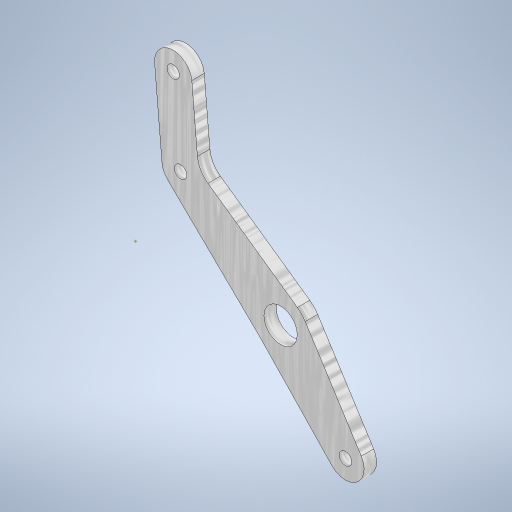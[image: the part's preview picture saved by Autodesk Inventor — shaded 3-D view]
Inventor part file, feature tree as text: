
AUTODESK INVENTOR PART (.ipt)
format: ipt  version: 2023 (Build 270158000, 158)  size: 302,592 bytes
history: native  units: mm
features: extrude x1, sketch x1
ambient origin geometry x8: Origin, YZ Plane, XZ Plane, XY Plane, X Axis, Y Axis, Z Axis, Center Point
bodies: Body1 (feature_tree)
feature tree (2):
  extrude  "Extrusion2"  [1 undecoded]
  sketch  "Sketch2"  dims[d23=3.0mm d24=0.0mm d25=3.0mm d26=9.0mm d27=8.05mm d28=14.05mm d29=3.0mm d30=9.0mm d31=3.0mm d32=9.0mm d33=40.0mm d34=20.0mm d35=20.0mm d36=6.0mm d37=2.0mm]
note: 1 required parameter value undecoded (feature->parameter linkage not recoverable at this tier; creation-order binding heuristic only, values carry confidence <= 0.55)
